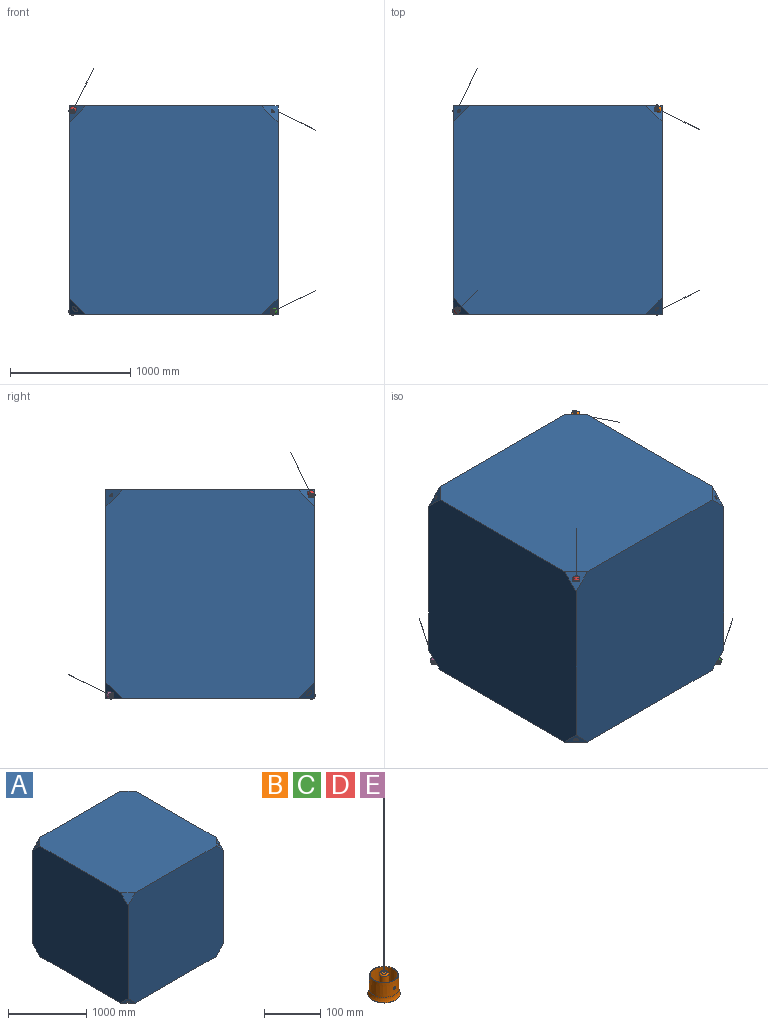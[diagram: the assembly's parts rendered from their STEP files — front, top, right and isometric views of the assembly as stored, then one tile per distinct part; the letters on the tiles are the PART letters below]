
ASSEMBLY  parts=5 mates=4
PART A: 22 faces, bbox 1731.8x1731.8x1731.8 mm
  f0: plane 1731.83x1731.83mm, normal (0,0,-1), area 2962733.6mm2, adj f1,f3,f4,f5,f7,f9,f11,f13
  f1: plane 1731.83x1731.83mm, normal (1,0,0), area 2962733.6mm2, adj f0,f2,f4,f5,f6,f7,f8,f9
  f2: plane 1731.83x1731.83mm, normal (0,0,1), area 2962733.6mm2, adj f1,f3,f4,f5,f6,f8,f10,f12
  f3: plane 1731.83x1731.83mm, normal (-1,0,0), area 2962733.6mm2, adj f0,f2,f4,f5,f10,f11,f12,f13
  f4: plane 1731.83x1731.83mm, normal (0,-1,0), area 2962733.6mm2, adj f0,f1,f2,f3,f6,f7,f10,f11
  f5: plane 1731.83x1731.83mm, normal (0,1,0), area 2962733.6mm2, adj f0,f1,f2,f3,f8,f9,f12,f13
  f6: plane 135.1x135.1mm, normal (0.58,-0.58,0.58), area 15178.2mm2, adj f1,f2,f4,f14
  f7: plane 135.1x135.1mm, normal (0.58,-0.58,-0.58), area 15806.7mm2, adj f0,f1,f4
  f8: plane 135.1x135.1mm, normal (0.58,0.58,0.58), area 15806.7mm2, adj f1,f2,f5
  f9: plane 135.1x135.1mm, normal (0.58,0.58,-0.58), area 13965.7mm2, adj f0,f1,f5,f20
  f10: plane 135.1x135.1mm, normal (-0.58,-0.58,0.58), area 15806.7mm2, adj f2,f3,f4
  f11: plane 135.1x135.1mm, normal (-0.58,-0.58,-0.58), area 13965.7mm2, adj f0,f3,f4,f18
  f12: plane 135.1x135.1mm, normal (-0.58,0.58,0.58), area 15178.2mm2, adj f2,f3,f5,f16
  f13: plane 135.1x135.1mm, normal (-0.58,0.58,-0.58), area 15806.7mm2, adj f0,f3,f5
  f14: cylinder r=14.14mm len=24.25mm, axis (-0.58,0.58,-0.58), area 177.7mm2, adj f6,f15
  f15: plane 23.1x23.1mm, normal (0.58,-0.58,0.58), area 628.5mm2, adj f14
  f16: cylinder r=14.14mm len=24.25mm, axis (0.58,-0.58,-0.58), area 177.7mm2, adj f12,f17
  f17: plane 23.1x23.1mm, normal (-0.58,0.58,0.58), area 628.5mm2, adj f16
  f18: cylinder r=24.21mm len=40.69mm, axis (0.58,0.58,0.58), area 304.2mm2, adj f11,f19
  f19: plane 39.53x39.53mm, normal (-0.58,-0.58,-0.58), area 1841mm2, adj f18
  f20: cylinder r=24.21mm len=40.69mm, axis (-0.58,-0.58,0.58), area 304.2mm2, adj f9,f21
  f21: plane 39.53x39.53mm, normal (0.58,0.58,-0.58), area 1841mm2, adj f20
PART B: 42 faces, bbox 73.1x73.1x447.4 mm
  f0: cylinder r=0.52mm len=393.7mm, axis (0,0,-1), area 1293.6mm2, adj f1,f13
  f1: plane 1.05x1.05mm, normal (0,0,1), area 0.9mm2, adj f0
  f2: cylinder r=2mm len=8.47mm, axis (0,1,0), area 105.7mm2, adj f3,f4,f7,f41
  f3: plane 3.86x1.48mm, normal (0,-1,0), area 4.2mm2, adj f2,f41
  f4: plane 3.86x1.48mm, normal (0,-1,0), area 4.2mm2, adj f2,f41
  f5: cone r=26.5mm half-angle=1.4deg, axis (0,0,-1), area 5010.3mm2, adj f23,f26,f37
  f6: cylinder r=2mm len=4mm, axis (0,1,0), area 12.2mm2, adj f8,f35
  f7: cylinder r=8.46mm len=26.16mm, axis (0,0,-1), area 1367.7mm2, adj f2,f9,f10,f11,f12,f15,f16,f27
  f8: cone r=25mm half-angle=0.7deg, axis (0,0,-1), area 4817.1mm2, adj f6,f9,f10,f11,f12,f22,f25,f27
  f9: extruded ~16.43x1.05mm, area 42.4mm2, adj f7,f8,f11,f12
  f10: extruded ~16.42x1.35mm, area 51.8mm2, adj f7,f8,f11,f12
  f11: plane 16.46x2.8mm, normal (0.46,0,0.89), area 51.7mm2, adj f7,f8,f9,f10
  f12: plane 16.47x2.8mm, normal (-0.46,0,-0.89), area 51.8mm2, adj f7,f8,f9,f10
  f13: plane 10.65x10.65mm, normal (0,0,1), area 88.3mm2, adj f0,f15
  f14: plane 14.93x14.93mm, normal (0,0,-1), area 170.2mm2, adj f16,f17
  f15: torus R=5.33mm, axis (0,0,1), area 226.9mm2, adj f7,f13
  f16: torus R=7.46mm, axis (0,0,1), area 80mm2, adj f7,f14
  f17: cylinder r=1.24mm len=5mm, axis (0,0,1), area 39mm2, adj f14,f18
  f18: plane 2.48x2.48mm, normal (0,0,-1), area 4mm2, adj f17,f40
  f19: plane 56.42x56.42mm, normal (0,0,-1), area 162.4mm2, adj f21,f24
  f20: plane 50.16x50.16mm, normal (0,0,1), area 1mm2, adj f25,f26
  f21: cone r=27.28mm half-angle=24.5deg, axis (0,0,-1), area 20.2mm2, adj f19,f22
  f22: torus R=50.44mm, axis (0,0,-1), area 1712.9mm2, adj f8,f21
  f23: torus R=51.85mm, axis (0,0,-1), area 1759.4mm2, adj f5,f24
  f24: torus R=28.21mm, axis (0,0,-1), area 179.5mm2, adj f19,f23
  f25: torus R=25.08mm, axis (0,0,1), area 123.1mm2, adj f8,f20
  f26: torus R=25.08mm, axis (0,0,1), area 123.3mm2, adj f5,f20
  f27: extruded ~14.76x9.12mm, area 42.4mm2, adj f7,f8,f28,f30
  f28: plane 15.61x10.64mm, normal (-0.23,0.4,0.89), area 51.7mm2, adj f7,f8,f27,f29
  f29: extruded ~14.89x9.38mm, area 51.8mm2, adj f7,f8,f28,f30
  f30: plane 15.62x10.65mm, normal (0.23,-0.4,-0.89), area 51.8mm2, adj f7,f8,f27,f29
  f31: extruded ~14.76x9.12mm, area 42.4mm2, adj f7,f8,f32,f34
  f32: plane 15.63x10.63mm, normal (-0.23,-0.4,0.89), area 51.7mm2, adj f7,f8,f31,f33
  f33: extruded ~14.89x9.38mm, area 51.8mm2, adj f7,f8,f32,f34
  f34: plane 15.64x10.64mm, normal (0.23,0.4,-0.89), area 51.8mm2, adj f7,f8,f31,f33
  f35: plane 4x4mm, normal (0,1,0), area 0.3mm2, adj f6,f36
  f36: cylinder r=1.98mm len=3.96mm, axis (0,1,0), area 5mm2, adj f35,f38
  f37: cylinder r=2.65mm len=5.31mm, axis (0,1,0), area 3.3mm2, adj f5,f38
  f38: plane 5.31x5.31mm, normal (0,-1,0), area 9.8mm2, adj f36,f37
  f39: plane 1.05x1.05mm, normal (0,0,-1), area 0.9mm2, adj f40
  f40: cylinder r=0.52mm len=11mm, axis (0,0,-1), area 36.1mm2, adj f18,f39
  f41: cylinder r=0.52mm len=3.93mm, axis (0,0,-1), area 6.4mm2, adj f2,f3,f4
PART C: same geometry as B
PART D: same geometry as B
PART E: same geometry as B
PLACE A t=(-281.63,526.63,166.45)mm fixed
PLACE B rot(axis=(0.54,0.84,0.07),114.7deg) t=(534.02,1372.7,1012.63)mm
PLACE C rot(axis=(-0.61,0.07,-0.79),125.8deg) t=(534.02,-319.59,-679.58)mm
PLACE D rot(axis=(0.13,0.3,0.95),137.1deg) t=(-1127.89,-319.37,982.1)mm
PLACE E rot(axis=(-0.74,0.59,0.31),69.7deg) t=(-1127.73,1342.28,-679.7)mm
MATE revolute B.f2 <-> A.f18  axis (-0.58,-0.58,-0.58) through (539.25,1347.51,987.33)mm
MATE revolute C.f2 <-> A.f16  axis (-0.58,0.58,0.58) through (539.25,-294.25,-654.43)mm
MATE revolute E.f2 <-> A.f14  axis (0.58,-0.58,0.58) through (-1102.51,1347.51,-654.43)mm
MATE revolute D.f2 <-> A.f20  axis (0.58,0.58,-0.58) through (-1102.51,-294.25,987.33)mm
